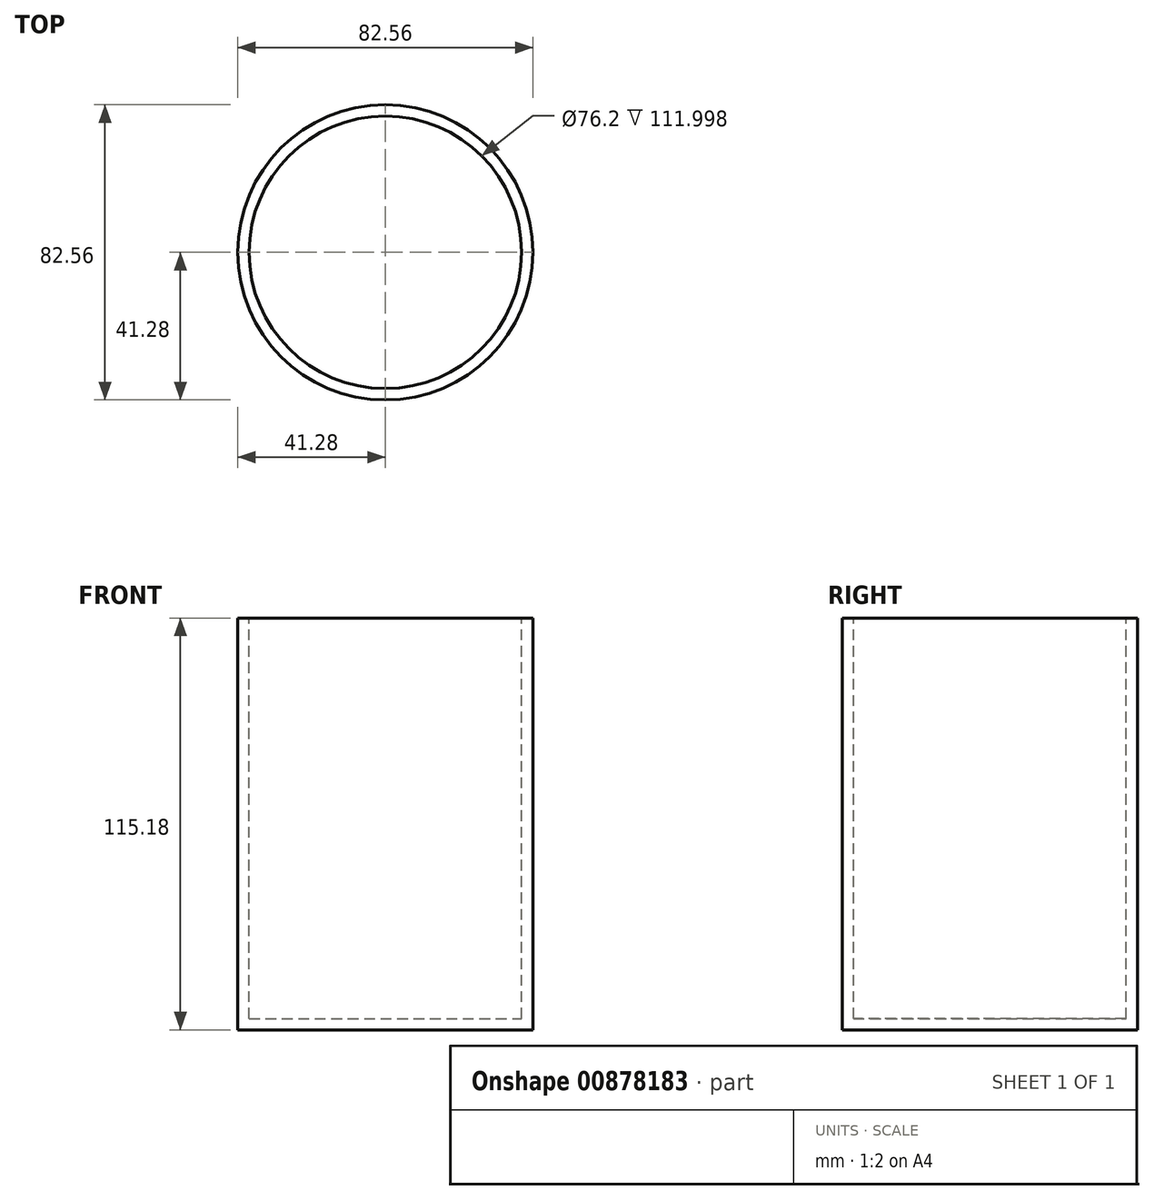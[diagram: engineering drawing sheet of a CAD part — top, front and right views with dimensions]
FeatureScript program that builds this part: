
annotation { "Feature Type Name" : "Feature", "Feature Type Description" : "" }
export const myFeature = defineFeature(function(context is Context, id is Id, definition is map)
    precondition{}
    {
        {
            var Q0;
            Q0=qCreatedBy(makeId("Front.planeOp"),FACE);
            var sketch = newSketch(context, id + "F0", { "sketchPlane" : qUnion([Q0])});
            skLineSegment(sketch, "E0.bottom", {"start": v(-41.28, 48.37) * mm, "end": v(0, 48.37) * mm});
            skLineSegment(sketch, "E0.top", {"start": v(-41.28, -66.8) * mm, "end": v(0, -66.8) * mm});
            skLineSegment(sketch, "E0.left", {"start": v(-41.28, 48.37) * mm, "end": v(-41.28, -66.8) * mm});
            skLineSegment(sketch, "E0.right", {"start": v(0, 48.37) * mm, "end": v(0, -66.8) * mm});
            skLineSegment(sketch, "E1", {"start": v(0, 90.35) * mm, "end": v(0, -91.2) * mm, "construction": true});
            skSolve(sketch);
        }
        {
            var Q0;
            Q0=makeQuery(id+"F0.imprint","IMPRINT",FACE,{"disambiguationData":[TD([[makeQuery(id+"F0.imprint","IMPRINT",EDGE,{"derivedFrom":sQuery(id+"F0.wireOp",EDGE,"E0.bottom")}),-1.0]])]});
            var Q1;
            Q1=sQuery(id+"F0.wireOp",EDGE,"E1");
            revolve(context, id + "F1", {"surfaceOperationType" : NewSurfaceOperationType.NEW, "entities" : qUnion([Q0]), "axis" : qUnion([Q1]), "revolveType" : RevolveType.FULL});
        }
        {
            var Q0;
            Q0=makeQuery(id+"F1.opRevolve","SWEPT_FACE",FACE,{"disambiguationData":[OSD([sQuery(id+"F0.wireOp",EDGE,"E0.bottom")])]});
            shell(context, id + "F2", {"entities" : qUnion([Q0]), "thickness" : 3.17 * mm});
        }
    });
